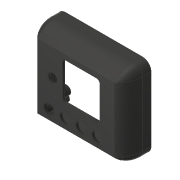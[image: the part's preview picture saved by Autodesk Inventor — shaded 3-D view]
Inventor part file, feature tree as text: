
AUTODESK INVENTOR PART (.ipt)
format: ipt  version: 2017 (Build 210142000, 142)  size: 659,456 bytes
history: native  units: in
note: dims shown in document units (in); Inventor stores cm internally (conversion verified against a paired STEP export)
features: sketch x29, projected_geometry x20, extrude x19, reference x16, other x10, plane x9, revolve x8
ambient origin geometry x8: Origin, YZ Plane, XZ Plane, XY Plane, X Axis, Y Axis, Z Axis, Center Point
bodies: Solid1 (feature_tree)
feature tree (111):
  sketch  "Sketch1"  dims[d0=1.0in d1=0.0in d4=0.02in]
  plane  "Work Plane1"
  extrude  "Extrusion1"  Depth=0.02in
  extrude  "Extrusion3"  Depth=0.02in
  extrude  "Extrusion4"  Depth=0.0625in TaperAngle=0.0deg
  extrude  "Extrusion5"  Depth=0.125in TaperAngle=0.0deg
  plane  "Work Plane2"
  extrude  "Extrusion7"  Depth=0.26in
  extrude  "Extrusion8"  Depth=0.26in
  plane  "Work Plane3"
  extrude  "Extrusion9"  Depth=1.0in TaperAngle=0.0deg
  revolve  "Revolution1"  [1 undecoded]
  revolve  "Revolution2"  [1 undecoded]
  revolve  "Revolution3"  [1 undecoded]
  revolve  "Revolution4"  [1 undecoded]
  extrude  "Extrusion10"  TaperAngle=90.0deg  [1 undecoded]
  extrude  "Extrusion11"  TaperAngle=90.0deg  [1 undecoded]
  extrude  "Extrusion12"  Depth=0.25in TaperAngle=0.0deg
  sketch  "Sketch18"  dims[d43=0.25in d44=0.0in d45=0.02in d46=0.0in]
  plane  "Work Plane4"
  extrude  "Extrusion13"  Depth=0.02in TaperAngle=0.0deg
  sketch  "Sketch19"  dims[d47=0.2in d48=0.2in]
  plane  "Work Plane5"
  extrude  "Extrusion14"  Depth=0.2in
  extrude  "Extrusion15"  Depth=0.02in TaperAngle=0.0deg
  plane  "Work Plane6"
  sketch  "Sketch23"  dims[d52=0.25in d53=0.1in]
  revolve  "Revolution5"  [1 undecoded]
  plane  "Work Plane7"
  revolve  "Revolution6"  [1 undecoded]
  plane  "Work Plane8"
  revolve  "Revolution7"  [1 undecoded]
  plane  "Work Plane9"
  revolve  "Revolution8"  [1 undecoded]
  extrude  "Extrusion18"  TaperAngle=90.0deg  [1 undecoded]
  extrude  "Extrusion19"  TaperAngle=90.0deg  [1 undecoded]
  extrude  "Extrusion20"  TaperAngle=0.0deg  [1 undecoded]
  extrude  "Extrusion21"  Depth=0.1in
  sketch  "Sketch32"  dims[d83=1.0in d84=0.0in d85=0.462in]
  extrude  "Extrusion22"  Depth=1.0in TaperAngle=0.0deg
  extrude  "Extrusion23"  Depth=0.462in
  sketch  "Sketch2"  dims[d5=0.02in d6=0.02in]
  reference  "Reference1"
  reference  "Reference2"
  reference  "Reference3"
  reference  "Reference4"
  reference  "Reference5"
  reference  "Reference6"
  reference  "Reference7"
  reference  "Reference8"
  reference  "Reference9"
  reference  "Reference10"
  reference  "Reference11"
  reference  "Reference12"
  sketch  "Sketch4"  dims[d7=0.02in d8=0.0625in d9=0.0in]
  sketch  "Sketch5"  dims[d10=0.02in d11=0.02in d12=0.02in d13=0.02in d14=0.125in d15=0.0in]
  sketch  "Sketch7"  dims[d16=0.26in d17=0.26in]
  sketch  "Sketch8"  dims[d18=0.26in d19=0.26in]
  sketch  "Sketch10"  dims[d20=0.26in d21=1.0in d22=0.0in]
  sketch  "Sketch11"  dims[d25=0.5in d26=0.25in]
  projected_geometry  "Projected Loop1"
  sketch  "Sketch12"  dims[d27=0.25in d28=0.25in]
  projected_geometry  "Projected Loop2"
  sketch  "Sketch13"  dims[d29=0.25in d30=0.0625in]
  projected_geometry  "Projected Loop3"
  sketch  "Sketch14"  dims[d31=0.25in d32=0.0in d33=0.25in d34=0.0in]
  projected_geometry  "Projected Loop4"
  sketch  "Sketch15"  dims[d35=0.25in d36=0.0in d37=90.0deg]
  projected_geometry  "Projected Loop5"
  projected_geometry  "Projected Loop6"
  projected_geometry  "Projected Loop7"
  projected_geometry  "Projected Loop8"
  sketch  "Sketch16"  dims[d38=90.0deg d39=90.0deg]
  projected_geometry  "Projected Loop9"
  projected_geometry  "Projected Loop10"
  projected_geometry  "Projected Loop11"
  projected_geometry  "Projected Loop12"
  sketch  "Sketch17"  dims[d40=90.0deg d41=0.25in d42=0.0in]
  reference  "Reference13"
  reference  "Reference14"
  reference  "Reference15"
  sketch  "Sketch20"  dims[d49=0.25in d50=0.02in d51=0.0in]
  sketch  "Sketch24"  dims[d54=0.02in d55=0.0in d56=0.23in]
  sketch  "Sketch25"  dims[d60=0.1in d61=0.1in]
  sketch  "Sketch26"  dims[d62=0.1in d63=0.1in]
  sketch  "Sketch27"  dims[d64=1.0in d65=0.0in d70=90.0deg]
  sketch  "Sketch28"  dims[d71=90.0deg d72=90.0deg]
  projected_geometry  "Projected Loop14"
  projected_geometry  "Projected Loop15"
  projected_geometry  "Projected Loop16"
  projected_geometry  "Projected Loop17"
  projected_geometry  "Projected Loop18"
  sketch  "Sketch29"  dims[d73=90.0deg d74=0.0in d75=0.0in]
  projected_geometry  "Projected Loop19"
  projected_geometry  "Projected Loop20"
  projected_geometry  "Projected Loop21"
  sketch  "Sketch30"  dims[d76=1.0in d77=0.0in d78=0.1in]
  sketch  "Sketch31"  dims[d79=0.25in d80=0.0in d81=1.0in d82=0.0in]
  reference  "Reference16"
  sketch  "Sketch33"  dims[d86=0.462in]
  sketch  "Sketch34"  dims[d87=0.462in d88=1.0in d89=0.0in d90=0.3in]
  parser-record x1  (decoder bookkeeping rows leaked as tree rows — omitted from the tree; the rows remain in map.json)
  other  "Assembly1.iam"
  other  "Button:1"
  other  "Button:2"
  other  "Button:3"
  other  "Button:4"
  other  "Button:5"
  other  "Power switch:1"
  other  "Control Board:1"
  other  "Main PCB:1"
note: 13 required parameter values undecoded (feature->parameter linkage not recoverable at this tier; creation-order binding heuristic only, values carry confidence <= 0.55)
note: 1 file-system path scrubbed to <path> (originals preserved in map.json)